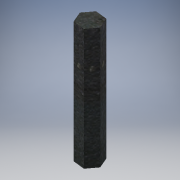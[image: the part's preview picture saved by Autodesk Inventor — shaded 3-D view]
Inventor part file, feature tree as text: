
AUTODESK INVENTOR PART (.ipt)
format: ipt  version: 2016 (Build 200138000, 138)  size: 104,960 bytes
history: native  units: in
note: dims shown in document units (in); Inventor stores cm internally (conversion verified against a paired STEP export)
features: extrude x1, sketch x1
ambient origin geometry x8: Origin, YZ Plane, XZ Plane, XY Plane, X Axis, Y Axis, Z Axis, Center Point
bodies: Solid1 (feature_tree)
feature tree (2):
  extrude  "Extrusion1"  Depth=3.0in TaperAngle=0.0deg
  sketch  "Sketch1"  dims[d0=0.5in d1=3.0in d2=0.0in]
